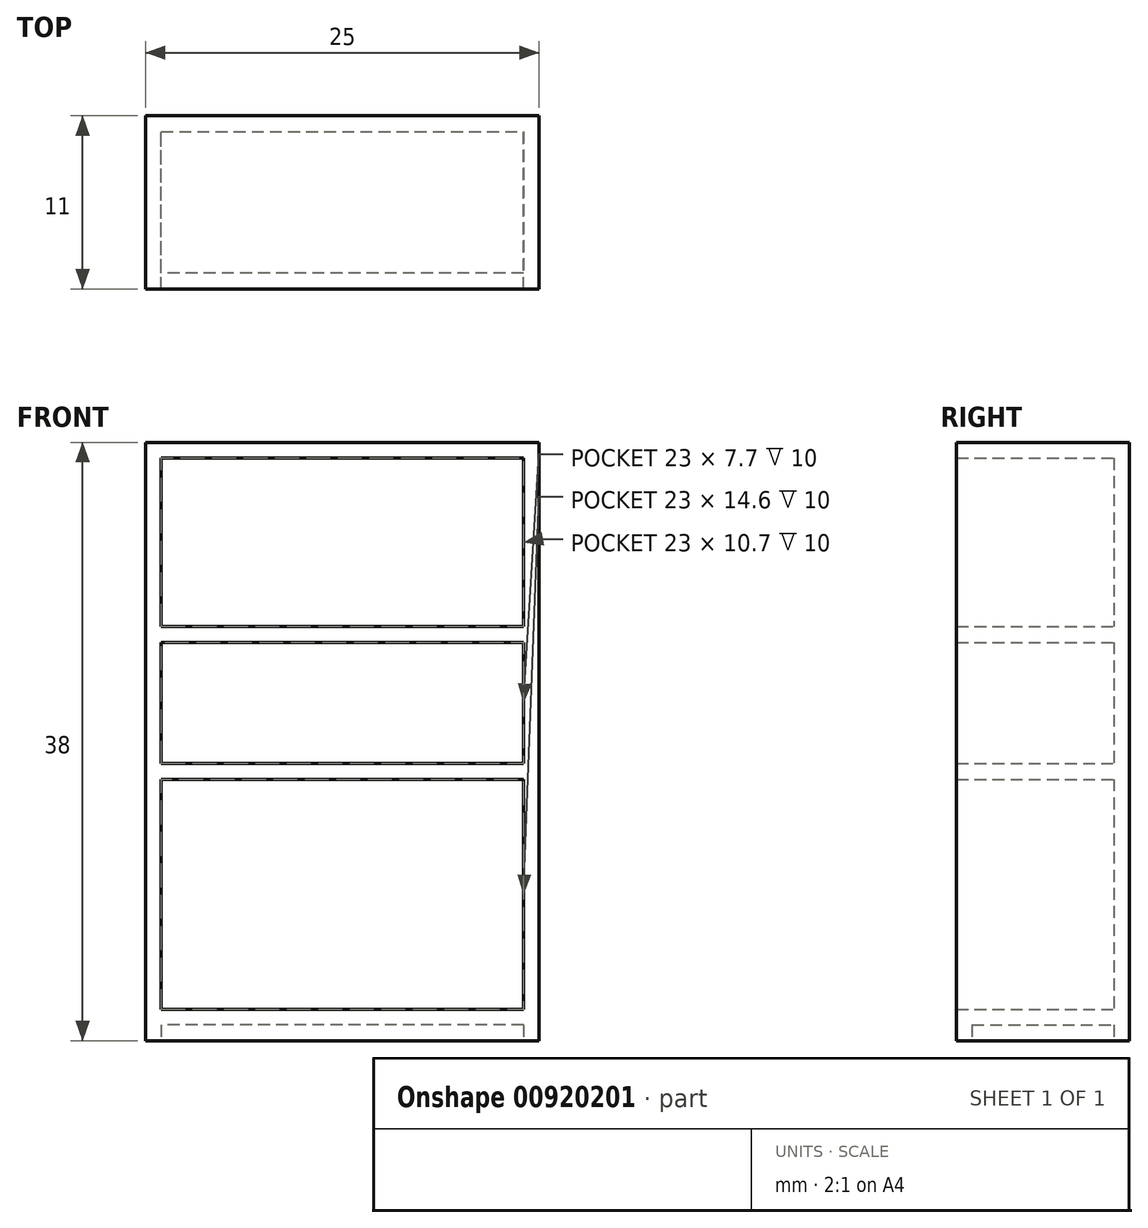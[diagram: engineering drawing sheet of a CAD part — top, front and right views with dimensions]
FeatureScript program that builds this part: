
annotation { "Feature Type Name" : "Feature", "Feature Type Description" : "" }
export const myFeature = defineFeature(function(context is Context, id is Id, definition is map)
    precondition{}
    {
        {
            var Q0;
            Q0=qCreatedBy(makeId("Front.planeOp"),FACE);
            var sketch = newSketch(context, id + "F0", { "sketchPlane" : qUnion([Q0])});
            skLineSegment(sketch, "E0.bottom", {"start": v(-12.5, 19) * mm, "end": v(12.5, 19) * mm});
            skLineSegment(sketch, "E0.top", {"start": v(-12.5, -19) * mm, "end": v(12.5, -19) * mm});
            skLineSegment(sketch, "E0.left", {"start": v(-12.5, 19) * mm, "end": v(-12.5, -19) * mm});
            skLineSegment(sketch, "E0.right", {"start": v(12.5, 19) * mm, "end": v(12.5, -19) * mm});
            skLineSegment(sketch, "E1.0", {"start": v(-11.5, 18) * mm, "end": v(11.5, 18) * mm});
            skLineSegment(sketch, "E1.1", {"start": v(-11.5, 18) * mm, "end": v(-11.5, 7.3) * mm});
            skLineSegment(sketch, "E1.2", {"start": v(-11.5, -18) * mm, "end": v(11.5, -18) * mm});
            skLineSegment(sketch, "E1.3", {"start": v(11.5, 18) * mm, "end": v(11.5, 7.3) * mm});
            skLineSegment(sketch, "E2.bottom", {"start": v(-11.5, 7.3) * mm, "end": v(11.5, 7.3) * mm});
            skLineSegment(sketch, "E2.top", {"start": v(-11.5, 6.3) * mm, "end": v(11.5, 6.3) * mm});
            skLineSegment(sketch, "E3.bottom", {"start": v(-11.5, -1.4) * mm, "end": v(11.5, -1.4) * mm});
            skLineSegment(sketch, "E3.top", {"start": v(-11.5, -2.4) * mm, "end": v(11.5, -2.4) * mm});
            skLineSegment(sketch, "E4.trimOffspring", {"start": v(11.5, 6.3) * mm, "end": v(11.5, -1.4) * mm});
            skLineSegment(sketch, "E5.trimOffspring", {"start": v(11.5, -2.4) * mm, "end": v(11.5, -18) * mm});
            skLineSegment(sketch, "E6.trimOffspring", {"start": v(-11.5, -2.4) * mm, "end": v(-11.5, -18) * mm});
            skLineSegment(sketch, "E7.trimOffspring", {"start": v(-11.5, 6.3) * mm, "end": v(-11.5, -1.4) * mm});
            skSolve(sketch);
        }
        {
            var Q0;
            Q0=makeQuery(id+"F0.imprint","IMPRINT",FACE,{"disambiguationData":[TD([[makeQuery(id+"F0.imprint","IMPRINT",EDGE,{"derivedFrom":sQuery(id+"F0.wireOp",EDGE,"E0.bottom")}),-1.0]])]});
            var Q1;
            Q1=makeQuery(id+"F0.imprint","IMPRINT",FACE,{"disambiguationData":[TD([[makeQuery(id+"F0.imprint","IMPRINT",EDGE,{"derivedFrom":sQuery(id+"F0.wireOp",EDGE,"E2.bottom")}),-1.0]])]});
            var Q2;
            Q2=makeQuery(id+"F0.imprint","IMPRINT",FACE,{"disambiguationData":[TD([[makeQuery(id+"F0.imprint","IMPRINT",EDGE,{"derivedFrom":sQuery(id+"F0.wireOp",EDGE,"E3.bottom")}),-1.0]])]});
            extrude(context, id + "F1", {"entities" : qUnion([Q0, Q1, Q2]), "depth" : 10 * mm, "offsetDistance" : 25 * mm});
        }
        {
            var Q0;
            Q0=makeQuery(id+"F1.opExtrude","CAP_FACE",FACE,{"disambiguationData":[OSD([sQuery(id+"F0.wireOp",EDGE,"E0.bottom"),sQuery(id+"F0.wireOp",EDGE,"E0.top"),sQuery(id+"F0.wireOp",EDGE,"E0.left"),sQuery(id+"F0.wireOp",EDGE,"E0.right"),sQuery(id+"F0.wireOp",EDGE,"E1.0"),sQuery(id+"F0.wireOp",EDGE,"E1.1"),sQuery(id+"F0.wireOp",EDGE,"E1.2"),sQuery(id+"F0.wireOp",EDGE,"E1.3"),sQuery(id+"F0.wireOp",EDGE,"E2.bottom"),sQuery(id+"F0.wireOp",EDGE,"E2.top"),sQuery(id+"F0.wireOp",EDGE,"E3.bottom"),sQuery(id+"F0.wireOp",EDGE,"E3.top"),sQuery(id+"F0.wireOp",EDGE,"E4.trimOffspring"),sQuery(id+"F0.wireOp",EDGE,"E5.trimOffspring"),sQuery(id+"F0.wireOp",EDGE,"E6.trimOffspring"),sQuery(id+"F0.wireOp",EDGE,"E7.trimOffspring")])],"isStart":true});
            var sketch = newSketch(context, id + "F2", { "sketchPlane" : qUnion([Q0])});
            skLineSegment(sketch, "E8.bottom", {"start": v(-12.5, 19) * mm, "end": v(12.5, 19) * mm});
            skLineSegment(sketch, "E8.top", {"start": v(-12.5, -19) * mm, "end": v(12.5, -19) * mm});
            skLineSegment(sketch, "E8.left", {"start": v(-12.5, 19) * mm, "end": v(-12.5, -19) * mm});
            skLineSegment(sketch, "E8.right", {"start": v(12.5, 19) * mm, "end": v(12.5, -19) * mm});
            skSolve(sketch);
        }
        {
            var Q0;
            Q0=makeQuery(id+"F2.imprint","IMPRINT",FACE,{"disambiguationData":[TD([[makeQuery(id+"F2.imprint","IMPRINT",EDGE,{"derivedFrom":sQuery(id+"F2.wireOp",EDGE,"E8.bottom")}),1.0]])]});
            var Q1;
            Q1=makeQuery(id+"F2.imprint","IMPRINT",FACE,{"disambiguationData":[TD([[makeQuery(id+"F2.imprint","IMPRINT",EDGE,{"derivedFrom":makeQuery(id+"F1.opExtrude","CAP_EDGE",EDGE,{"disambiguationData":[OSD([sQuery(id+"F0.wireOp",EDGE,"E1.2")])],"isStart":true})}),-1.0]])]});
            var Q2;
            Q2=makeQuery(id+"F2.imprint","IMPRINT",FACE,{"disambiguationData":[TD([[makeQuery(id+"F2.imprint","IMPRINT",EDGE,{"derivedFrom":makeQuery(id+"F1.opExtrude","CAP_EDGE",EDGE,{"disambiguationData":[OSD([sQuery(id+"F0.wireOp",EDGE,"E1.0")])],"isStart":true})}),1.0]])]});
            var Q3;
            Q3=makeQuery(id+"F2.imprint","IMPRINT",FACE,{"disambiguationData":[TD([[makeQuery(id+"F2.imprint","IMPRINT",EDGE,{"derivedFrom":makeQuery(id+"F1.opExtrude","CAP_EDGE",EDGE,{"disambiguationData":[OSD([sQuery(id+"F0.wireOp",EDGE,"E2.top")])],"isStart":true})}),1.0]])]});
            extrude(context, id + "F3", {"entities" : qUnion([Q0, Q1, Q2, Q3]), "operationType" : NewBodyOperationType.ADD, "depth" : 1 * mm, "offsetDistance" : 25 * mm});
        }
        {
            var Q0;
            Q0=makeQuery(id+"F1.opExtrude","SWEPT_FACE",FACE,{"disambiguationData":[OSD([sQuery(id+"F0.wireOp",EDGE,"E1.2")])]});
            extrude(context, id + "F4", {"entities" : qUnion([Q0]), "operationType" : NewBodyOperationType.ADD, "depth" : 1 * mm, "offsetDistance" : 25 * mm});
        }
        {
            var Q0;
            Q0=makeQuery(id+"F3.boolean.opBoolean","MERGE",FACE,{"derivedFrom":[makeQuery(id+"F1.opExtrude","SWEPT_FACE",FACE,{"disambiguationData":[OSD([sQuery(id+"F0.wireOp",EDGE,"E0.top")])]}),makeQuery(id+"F3.opExtrude","SWEPT_FACE",FACE,{"disambiguationData":[OSD([sQuery(id+"F2.wireOp",EDGE,"E8.top")])]})]});
            var sketch = newSketch(context, id + "F5", { "sketchPlane" : qUnion([Q0])});
            skLineSegment(sketch, "E9.0", {"start": v(-11.5, 9) * mm, "end": v(-11.5, 0) * mm});
            skLineSegment(sketch, "E9.1", {"start": v(11.5, 9) * mm, "end": v(-11.5, 9) * mm});
            skLineSegment(sketch, "E9.2", {"start": v(11.5, 0) * mm, "end": v(11.5, 9) * mm});
            skLineSegment(sketch, "E9.3", {"start": v(-11.5, 0) * mm, "end": v(11.5, 0) * mm});
            skSolve(sketch);
        }
        {
            var Q0;
            Q0=makeQuery(id+"F5.imprint","IMPRINT",FACE,{"disambiguationData":[TD([[makeQuery(id+"F5.imprint","IMPRINT",EDGE,{"derivedFrom":sQuery(id+"F5.wireOp",EDGE,"E9.0")}),1.0]])]});
            extrude(context, id + "F6", {"entities" : qUnion([Q0]), "operationType" : NewBodyOperationType.REMOVE, "oppositeDirection" : true, "depth" : 1 * mm, "offsetDistance" : 25 * mm});
        }
    });
